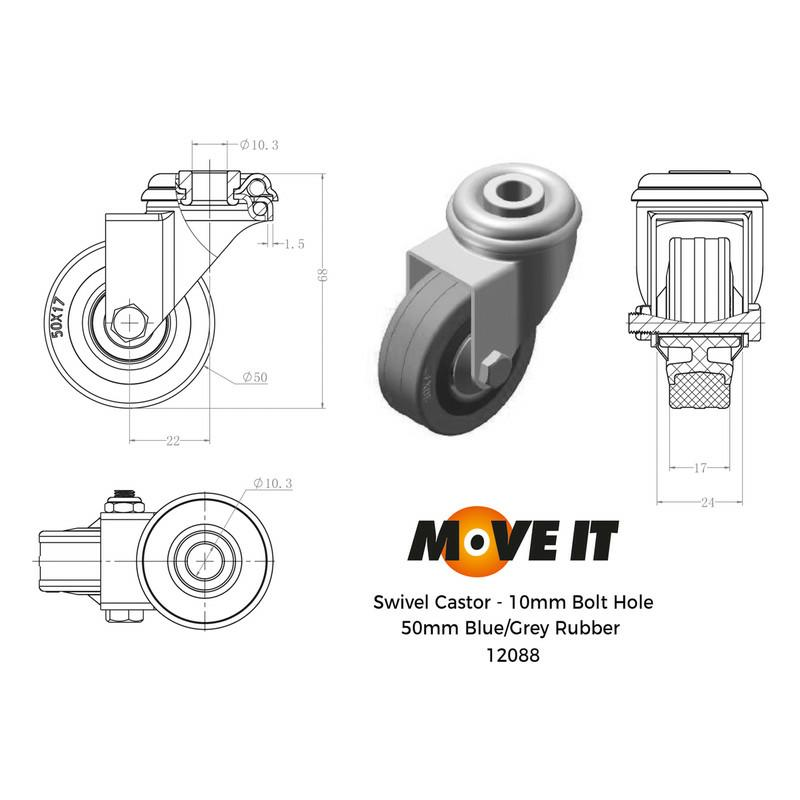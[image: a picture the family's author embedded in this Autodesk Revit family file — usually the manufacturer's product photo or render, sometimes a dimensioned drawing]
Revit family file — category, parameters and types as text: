
# Revit family: AV Divider 1200
name_source: partatom
category: Generic Models
units: mm (PartAtom-declared; Revit-internal decimal feet)

## family parameters
Always vertical = Yes
Can host rebar = No
Cut with Voids When Loaded = No
Maintain Annotation Orientation = No
Part Type = Normal
Room Calculation Point = No
Round Connector Dimension = Use Diameter
Shared = No
Work Plane-Based = No

## types (1)
- ThinkingWall® AV Divider
    Default Elevation = 0 mm  [stored 0 ft]
    Description = Double sided mobile whiteboard wall with large screen and connecting AV equipment. Part of the ThinkingWall® range for flexible breakout and meeting spaces.
    End Panel Colours = <By Category>
    Manufacturer = Logovisual LTD
    Model = ThinkingWall® AV Divider
    TV Height = 830 mm  [stored 2.7231 ft]
    TV Position = 1100 mm
    TV Position Top = 110 mm  [stored 0.360892 ft]
    TV Width = 1450 mm  [stored 4.75722 ft]
    URL = https://www.logovisual.com

note: [stored X ft] marks values corroborated as IEEE doubles in the binary element streams (Revit-internal decimal feet)

## geometry (parser evidence)
native form markers: Sweep x20
no freeform markers — native parametric forms only
